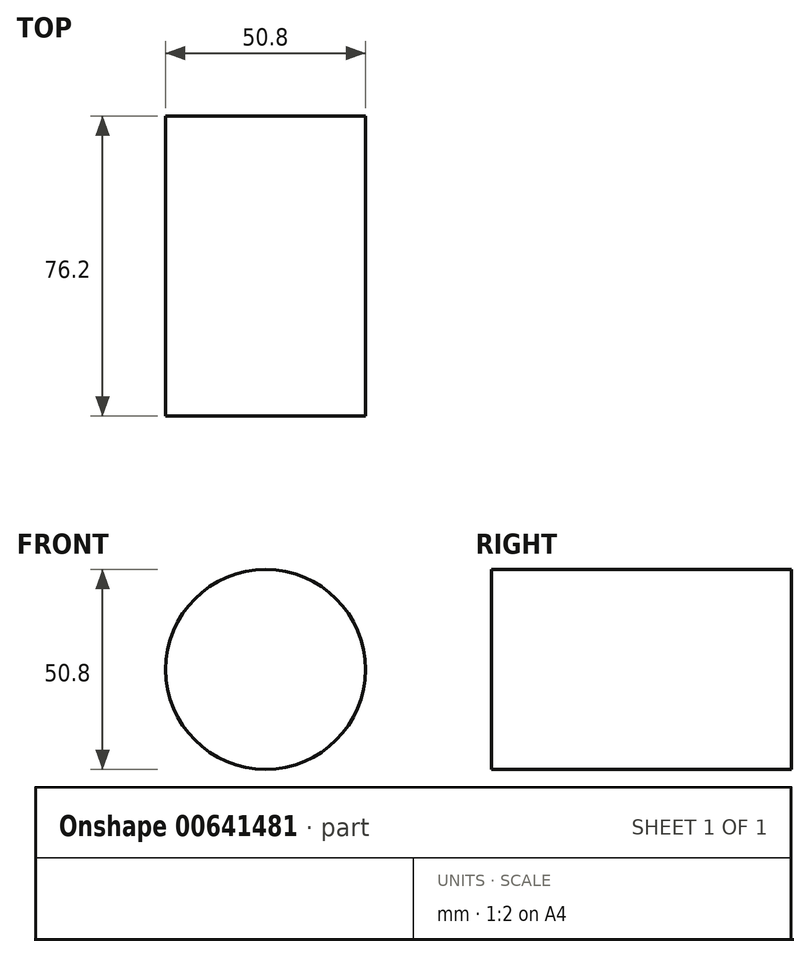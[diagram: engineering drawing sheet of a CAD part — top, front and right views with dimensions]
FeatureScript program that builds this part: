
annotation { "Feature Type Name" : "Feature", "Feature Type Description" : "" }
export const myFeature = defineFeature(function(context is Context, id is Id, definition is map)
    precondition{}
    {
        {
            var Q0;
            Q0=qCreatedBy(makeId("Front.planeOp"),FACE);
            var sketch = newSketch(context, id + "F0", { "sketchPlane" : qUnion([Q0])});
            skCircle(sketch, "E0", {"center": v(-33.73, 9.84) * mm, "radius": 25.4 * mm});
            skSolve(sketch);
        }
        {
            var Q0;
            Q0=makeQuery(id+"F0.imprint","IMPRINT",FACE,{"disambiguationData":[TD([[makeQuery(id+"F0.imprint","IMPRINT",EDGE,{"derivedFrom":sQuery(id+"F0.wireOp",EDGE,"E0")}),1.0]])]});
            extrude(context, id + "F1", {"entities" : qUnion([Q0]), "depth" : 76.2 * mm, "offsetDistance" : 25.4 * mm});
        }
    });
